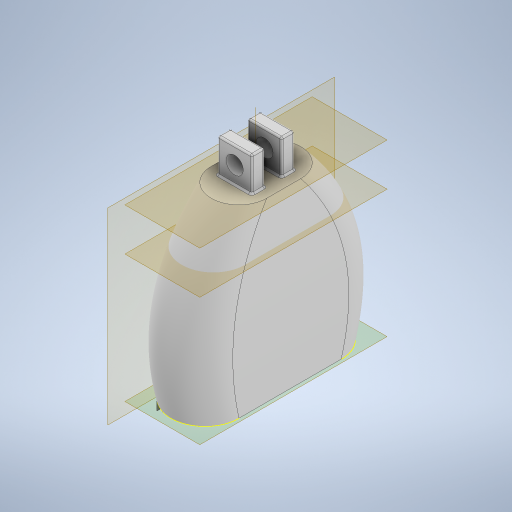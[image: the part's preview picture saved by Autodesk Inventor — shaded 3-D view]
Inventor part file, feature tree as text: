
AUTODESK INVENTOR PART (.ipt)
format: ipt  version: 2023 (Build 270158000, 158)  size: 561,152 bytes
history: native  units: mm
features: sketch x12, extrude x6, plane x4, chamfer x2, mirror x2, loft x1, shell x1, fillet x1, projected_geometry x1
ambient origin geometry x8: Origin, YZ Plane, XZ Plane, XY Plane, X Axis, Y Axis, Z Axis, Center Point
bodies: Solid1 (feature_tree)
feature tree (30):
  sketch  "Sketch1"  dims[d0=120.0mm d1=80.0mm d2=20.0mm]
  plane  "Work Plane1"
  sketch  "Sketch2"  dims[d3=200.0mm d4=40.0mm]
  plane  "Work Plane2"
  sketch  "Sketch3"  dims[d5=65.0mm d6=150.0mm]
  plane  "Work Plane3"
  loft  "Loft1"
  shell  "Shell1"  Thickness=20.0mm
  sketch  "Sketch4"  dims[d7=100.0mm d8=75.0mm]
  plane  "Work Plane4"
  extrude  "Extrusion1"  Depth=40.0mm
  sketch  "Sketch10"  dims[d15=3.0mm]
  extrude  "Extrusion2"  Depth=150.0mm
  sketch  "Sketch12"  dims[d22=40.0mm]
  extrude  "Extrusion3"  Depth=75.0mm
  extrude  "Extrusion4"  TaperAngle=0.0deg  [1 undecoded]
  fillet  "Fillet1"  [1 undecoded]
  chamfer  "Chamfer1"  Distance=10.0mm
  chamfer  "Chamfer2"  Distance=40.0mm
  extrude  "Extrusion5"  Depth=50.0mm TaperAngle=0.0deg
  extrude  "Extrusion7"  Depth=40.0mm TaperAngle=0.0deg
  mirror  "Mirror2"
  mirror  "Mirror3"
  sketch  "Sketch9"  dims[d9=0.0mm d10=90.0deg d11=0.0mm d12=90.0deg d13=0.0mm d14=90.0deg]
  projected_geometry  "Projected Loop1"
  sketch  "Sketch11"  dims[d19=21.0mm d20=10.0mm d21=0.0mm]
  sketch  "Sketch13"  dims[d23=50.0mm d24=40.0mm d25=0.0mm]
  sketch  "Sketch14"  dims[d26=20.0mm d27=50.0mm d28=0.0mm]
  sketch  "Sketch15"  dims[d29=20.0mm d30=40.0mm d31=0.0mm]
  sketch  "Sketch17"  dims[d32=2.0mm d33=2.0mm d34=2.0mm d35=45.0deg d36=2.0mm d37=2.0mm d38=45.0deg d39=55.0mm d40=25.0mm d41=12.5mm d42=5.0mm d43=5.0mm d44=2.0mm d45=2.0mm d46=10.0mm d47=0.0mm d55=4.0mm d56=5.0mm d57=4.0mm d58=10.0mm d59=0.0mm]
note: 2 required parameter values undecoded (feature->parameter linkage not recoverable at this tier; creation-order binding heuristic only, values carry confidence <= 0.55)
